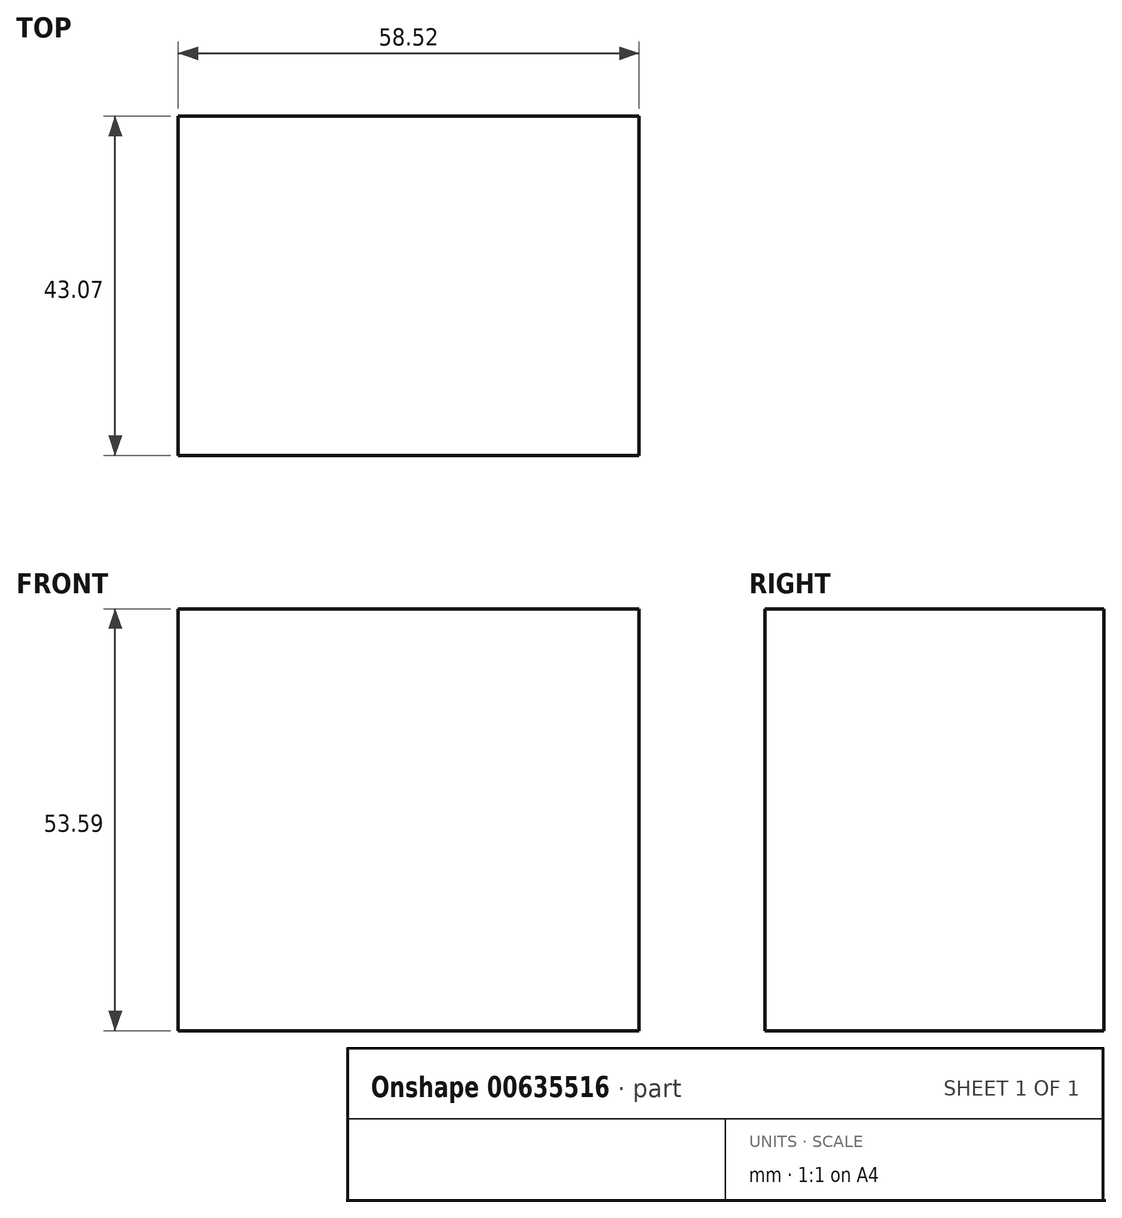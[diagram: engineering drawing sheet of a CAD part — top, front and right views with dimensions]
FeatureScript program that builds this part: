
annotation { "Feature Type Name" : "Feature", "Feature Type Description" : "" }
export const myFeature = defineFeature(function(context is Context, id is Id, definition is map)
    precondition{}
    {
        {
            var Q0;
            Q0=qCreatedBy(makeId("Top.planeOp"),FACE);
            var sketch = newSketch(context, id + "F0", { "sketchPlane" : qUnion([Q0])});
            skLineSegment(sketch, "E0.bottom", {"start": v(0, 0) * mm, "end": v(58.52, 0) * mm});
            skLineSegment(sketch, "E0.top", {"start": v(0, -43.07) * mm, "end": v(58.52, -43.07) * mm});
            skLineSegment(sketch, "E0.left", {"start": v(0, 0) * mm, "end": v(0, -43.07) * mm});
            skLineSegment(sketch, "E0.right", {"start": v(58.52, 0) * mm, "end": v(58.52, -43.07) * mm});
            skSolve(sketch);
        }
        {
            var Q0;
            Q0=makeQuery(id+"F0.imprint","IMPRINT",FACE,{"disambiguationData":[TD([[makeQuery(id+"F0.imprint","IMPRINT",EDGE,{"derivedFrom":sQuery(id+"F0.wireOp",EDGE,"E0.bottom")}),-1.0]])]});
            extrude(context, id + "F1", {"entities" : qUnion([Q0]), "depth" : 53.6 * mm, "offsetDistance" : 25.4 * mm});
        }
    });
